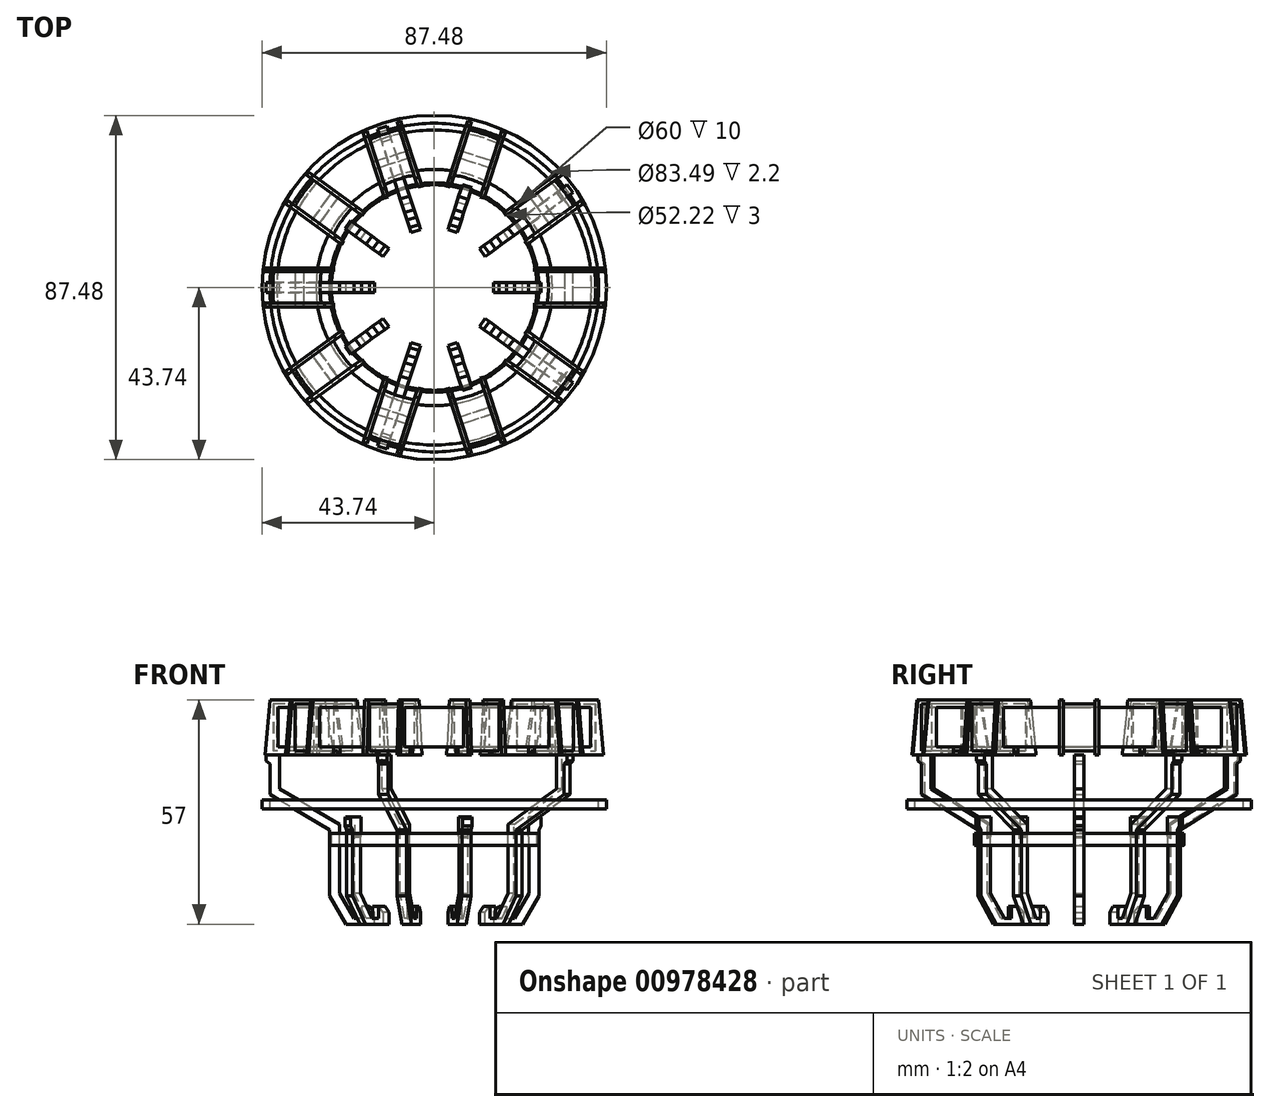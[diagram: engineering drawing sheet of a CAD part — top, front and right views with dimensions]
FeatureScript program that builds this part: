
annotation { "Feature Type Name" : "Feature", "Feature Type Description" : "" }
export const myFeature = defineFeature(function(context is Context, id is Id, definition is map)
    precondition{}
    {
        {
            var Q0;
            Q0=qCreatedBy(makeId("Top.planeOp"),FACE);
            var sketch = newSketch(context, id + "F0", { "sketchPlane" : qUnion([Q0])});
            skCircle(sketch, "E0", {"center": v(0, 0) * mm, "radius": 30 * mm});
            skCircle(sketch, "E1", {"center": v(0, 0) * mm, "radius": 40 * mm});
            skSolve(sketch);
        }
        {
            var Q0;
            Q0=makeQuery(id+"F0.imprint","IMPRINT",FACE,{"disambiguationData":[TD([[makeQuery(id+"F0.imprint","IMPRINT",EDGE,{"derivedFrom":sQuery(id+"F0.wireOp",EDGE,"E0")}),-1.0]])]});
            extrude(context, id + "F1", {"entities" : qUnion([Q0]), "depth" : 10 * mm, "offsetDistance" : 25 * mm});
        }
        {
            var Q0;
            Q0=qCreatedBy(makeId("Front.planeOp"),FACE);
            var sketch = newSketch(context, id + "F2", { "sketchPlane" : qUnion([Q0])});
            skLineSegment(sketch, "E2", {"start": v(-41.7, 12) * mm, "end": v(-27.87, 12) * mm});
            skLineSegment(sketch, "E3", {"start": v(-27.87, 12) * mm, "end": v(-25.51, -2) * mm});
            skLineSegment(sketch, "E4", {"start": v(-43.03, -2) * mm, "end": v(-41.7, 12) * mm});
            skLineSegment(sketch, "E5", {"start": v(-43.03, -2) * mm, "end": v(-35.17, -2) * mm});
            skLineSegment(sketch, "E6", {"start": v(-35.17, -2) * mm, "end": v(-35.17, 1.56) * mm});
            skLineSegment(sketch, "E7", {"start": v(-35.17, 1.56) * mm, "end": v(-33.24, 1.56) * mm});
            skLineSegment(sketch, "E8", {"start": v(-33.24, 1.56) * mm, "end": v(-33.24, -2) * mm});
            skLineSegment(sketch, "E9", {"start": v(-33.24, -2) * mm, "end": v(-25.51, -2) * mm});
            skSolve(sketch);
        }
        {
            var Q0;
            Q0 = qSketchRegion(id + "F2", true);
            extrude(context, id + "F3", {"entities" : qUnion([Q0]), "endBound" : BoundingType.SYMMETRIC, "depth" : 10 * mm, "offsetDistance" : 25 * mm});
        }
        {
            var Q0;
            Q0=makeQuery(id+"F1.opExtrude","SWEPT_BODY",BODY,{"disambiguationData":[OSD([sQuery(id+"F0.wireOp",EDGE,"E0"),sQuery(id+"F0.wireOp",EDGE,"E1")])]});
            var Q1;
            Q1=makeQuery(id+"F3.opExtrude","SWEPT_BODY",BODY,{"disambiguationData":[OSD([sQuery(id+"F2.wireOp",EDGE,"E2"),sQuery(id+"F2.wireOp",EDGE,"E3"),sQuery(id+"F2.wireOp",EDGE,"E4"),sQuery(id+"F2.wireOp",EDGE,"E5"),sQuery(id+"F2.wireOp",EDGE,"E6"),sQuery(id+"F2.wireOp",EDGE,"E7"),sQuery(id+"F2.wireOp",EDGE,"E8"),sQuery(id+"F2.wireOp",EDGE,"E9")])]});
            booleanBodies(context, id + "F4", {"operationType" : BooleanOperationType.SUBTRACTION, "tools" : qUnion([Q0]), "targets" : qUnion([Q1]), "keepTools" : true});
        }
        {
            var Q0;
            Q0=makeQuery(id+"F3.opExtrude","SWEPT_FACE",FACE,{"disambiguationData":[OSD([sQuery(id+"F2.wireOp",EDGE,"E2")])]});
            var Q1;
            Q1=makeQuery(id+"F3.opExtrude","SWEPT_FACE",FACE,{"disambiguationData":[OSD([sQuery(id+"F2.wireOp",EDGE,"E4")])]});
            var Q2;
            Q2=makeQuery(id+"F3.opExtrude","SWEPT_FACE",FACE,{"disambiguationData":[OSD([sQuery(id+"F2.wireOp",EDGE,"E5")])]});
            var Q3;
            Q3=makeQuery(id+"F3.opExtrude","SWEPT_FACE",FACE,{"disambiguationData":[OSD([sQuery(id+"F2.wireOp",EDGE,"E9")])]});
            var Q4;
            Q4=makeQuery(id+"F3.opExtrude","SWEPT_FACE",FACE,{"disambiguationData":[OSD([sQuery(id+"F2.wireOp",EDGE,"E3")])]});
            var Q5;
            Q5=makeQuery(id+"F3.opExtrude","SWEPT_FACE",FACE,{"disambiguationData":[OSD([sQuery(id+"F2.wireOp",EDGE,"E6")])]});
            var Q6;
            Q6=makeQuery(id+"F3.opExtrude","SWEPT_FACE",FACE,{"disambiguationData":[OSD([sQuery(id+"F2.wireOp",EDGE,"E8")])]});
            shell(context, id + "F5", {"entities" : qUnion([Q0, Q1, Q2, Q3, Q4, Q5, Q6]), "thickness" : 1 * mm});
        }
        {
            var Q0;
            Q0=makeQuery(id+"F3.opExtrude","SWEPT_BODY",BODY,{"disambiguationData":[OSD([sQuery(id+"F2.wireOp",EDGE,"E2"),sQuery(id+"F2.wireOp",EDGE,"E3"),sQuery(id+"F2.wireOp",EDGE,"E4"),sQuery(id+"F2.wireOp",EDGE,"E5"),sQuery(id+"F2.wireOp",EDGE,"E6"),sQuery(id+"F2.wireOp",EDGE,"E7"),sQuery(id+"F2.wireOp",EDGE,"E8"),sQuery(id+"F2.wireOp",EDGE,"E9")])]});
            var Q1;
            Q1=makeQuery(id+"F1.opExtrude","SWEPT_FACE",FACE,{"disambiguationData":[OSD([sQuery(id+"F0.wireOp",EDGE,"E0")])]});
            circularPattern(context, id + "F6", {"entities" : qUnion([Q0]), "axis" : qUnion([Q1]), "angle" : 360 * degree, "instanceCount" : 10, "equalSpace" : true});
        }
        {
            var Q0;
            Q0=qCreatedBy(makeId("Front.planeOp"),FACE);
            var sketch = newSketch(context, id + "F7", { "sketchPlane" : qUnion([Q0])});
            skLineSegment(sketch, "E10", {"start": v(15.1, -42) * mm, "end": v(15.1, -45) * mm});
            skLineSegment(sketch, "E11", {"start": v(15.1, -45) * mm, "end": v(22.45, -45) * mm});
            skLineSegment(sketch, "E12", {"start": v(22.45, -45) * mm, "end": v(26.6, -37.82) * mm});
            skLineSegment(sketch, "E13", {"start": v(26.6, -37.82) * mm, "end": v(26.6, -21.05) * mm});
            skLineSegment(sketch, "E14", {"start": v(26.6, -21.05) * mm, "end": v(27.15, -20.09) * mm});
            skLineSegment(sketch, "E15", {"start": v(27.15, -20.09) * mm, "end": v(27.15, -18.09) * mm});
            skLineSegment(sketch, "E16", {"start": v(26.96, -17.76) * mm, "end": v(27.15, -18.09) * mm});
            skLineSegment(sketch, "E17", {"start": v(26.96, -17.76) * mm, "end": v(23.96, -17.76) * mm});
            skLineSegment(sketch, "E18", {"start": v(15.1, -42) * mm, "end": v(16.42, -40.5) * mm});
            skLineSegment(sketch, "E19", {"start": v(16.42, -40.5) * mm, "end": v(18.42, -40.5) * mm});
            skLineSegment(sketch, "E20", {"start": v(18.42, -40.5) * mm, "end": v(18.42, -43.5) * mm});
            skLineSegment(sketch, "E21", {"start": v(24.1, -37.15) * mm, "end": v(24.1, -22.99) * mm});
            skLineSegment(sketch, "E22", {"start": v(24.1, -22.99) * mm, "end": v(23.96, -22.76) * mm});
            skLineSegment(sketch, "E23", {"start": v(23.96, -22.76) * mm, "end": v(23.96, -17.76) * mm});
            skLineSegment(sketch, "E24", {"start": v(18.42, -43.5) * mm, "end": v(20.42, -43.5) * mm});
            skLineSegment(sketch, "E25", {"start": v(20.42, -43.5) * mm, "end": v(24.1, -37.15) * mm});
            skLineSegment(sketch, "E26", {"start": v(-15.1, -45) * mm, "end": v(-15.1, -42) * mm});
            skLineSegment(sketch, "E27", {"start": v(-15.1, -42) * mm, "end": v(-16.42, -40.5) * mm});
            skLineSegment(sketch, "E28", {"start": v(-16.42, -40.5) * mm, "end": v(-18.42, -40.5) * mm});
            skLineSegment(sketch, "E29", {"start": v(-18.42, -40.5) * mm, "end": v(-18.42, -43.5) * mm});
            skLineSegment(sketch, "E30", {"start": v(-18.42, -43.5) * mm, "end": v(-20.42, -43.5) * mm});
            skLineSegment(sketch, "E31", {"start": v(-20.42, -43.5) * mm, "end": v(-24.1, -37.15) * mm});
            skLineSegment(sketch, "E32", {"start": v(-24.1, -37.15) * mm, "end": v(-24.1, -19.63) * mm});
            skLineSegment(sketch, "E33", {"start": v(-24.1, -19.63) * mm, "end": v(-39.24, -10.66) * mm});
            skLineSegment(sketch, "E34", {"start": v(-39.24, -10.66) * mm, "end": v(-39.24, -2) * mm});
            skLineSegment(sketch, "E35", {"start": v(-39.24, -2) * mm, "end": v(-42.68, -2) * mm});
            skLineSegment(sketch, "E36", {"start": v(-41.74, -4.3) * mm, "end": v(-41.74, -12.08) * mm});
            skLineSegment(sketch, "E37", {"start": v(-41.74, -12.08) * mm, "end": v(-26.6, -21.05) * mm});
            skLineSegment(sketch, "E38", {"start": v(-26.6, -21.05) * mm, "end": v(-26.6, -37.82) * mm});
            skLineSegment(sketch, "E39", {"start": v(-26.6, -37.82) * mm, "end": v(-22.45, -45) * mm});
            skLineSegment(sketch, "E40", {"start": v(-22.45, -45) * mm, "end": v(-15.1, -45) * mm});
            skLineSegment(sketch, "E41", {"start": v(-42.68, -2) * mm, "end": v(-42.68, -3.5) * mm});
            skLineSegment(sketch, "E42", {"start": v(-42.68, -3.5) * mm, "end": v(-41.74, -4.3) * mm});
            skSolve(sketch);
        }
        {
            var Q0;
            Q0=makeQuery(id+"F7.imprint","IMPRINT",FACE,{"disambiguationData":[TD([[makeQuery(id+"F7.imprint","IMPRINT",EDGE,{"derivedFrom":sQuery(id+"F7.wireOp",EDGE,"E10")}),1.0]])]});
            var Q1;
            Q1=makeQuery(id+"F7.imprint","IMPRINT",FACE,{"disambiguationData":[TD([[makeQuery(id+"F7.imprint","IMPRINT",EDGE,{"derivedFrom":sQuery(id+"F7.wireOp",EDGE,"E26")}),1.0]])]});
            extrude(context, id + "F8", {"entities" : qUnion([Q0, Q1]), "endBound" : BoundingType.SYMMETRIC, "depth" : 2.5 * mm, "offsetDistance" : 25 * mm});
        }
        {
            var Q0;
            Q0=makeQuery(id+"F8.opExtrude","SWEPT_BODY",BODY,{"disambiguationData":[OSD([sQuery(id+"F7.wireOp",EDGE,"E10"),sQuery(id+"F7.wireOp",EDGE,"E11"),sQuery(id+"F7.wireOp",EDGE,"E12"),sQuery(id+"F7.wireOp",EDGE,"E13"),sQuery(id+"F7.wireOp",EDGE,"E14"),sQuery(id+"F7.wireOp",EDGE,"E15"),sQuery(id+"F7.wireOp",EDGE,"E16"),sQuery(id+"F7.wireOp",EDGE,"E17"),sQuery(id+"F7.wireOp",EDGE,"E18"),sQuery(id+"F7.wireOp",EDGE,"E19"),sQuery(id+"F7.wireOp",EDGE,"E20"),sQuery(id+"F7.wireOp",EDGE,"E21"),sQuery(id+"F7.wireOp",EDGE,"E22"),sQuery(id+"F7.wireOp",EDGE,"E23"),sQuery(id+"F7.wireOp",EDGE,"E24"),sQuery(id+"F7.wireOp",EDGE,"E25")])]});
            var Q1;
            Q1=makeQuery(id+"F8.opExtrude","SWEPT_BODY",BODY,{"disambiguationData":[OSD([sQuery(id+"F7.wireOp",EDGE,"E26"),sQuery(id+"F7.wireOp",EDGE,"E27"),sQuery(id+"F7.wireOp",EDGE,"E28"),sQuery(id+"F7.wireOp",EDGE,"E29"),sQuery(id+"F7.wireOp",EDGE,"E30"),sQuery(id+"F7.wireOp",EDGE,"E31"),sQuery(id+"F7.wireOp",EDGE,"E32"),sQuery(id+"F7.wireOp",EDGE,"E33"),sQuery(id+"F7.wireOp",EDGE,"E34"),sQuery(id+"F7.wireOp",EDGE,"E35"),sQuery(id+"F7.wireOp",EDGE,"ou7bWfvp-Nuvi-0B3R-6LIp-XRIRuBnvQizE"),sQuery(id+"F7.wireOp",EDGE,"mc10MxTr-XRXP-W1Zo-hVJU-oox8hIU6NUmr"),sQuery(id+"F7.wireOp",EDGE,"E36"),sQuery(id+"F7.wireOp",EDGE,"E37"),sQuery(id+"F7.wireOp",EDGE,"E38"),sQuery(id+"F7.wireOp",EDGE,"E39"),sQuery(id+"F7.wireOp",EDGE,"E40")])]});
            var Q2;
            Q2=makeQuery(id+"F1.opExtrude","CAP_EDGE",EDGE,{"disambiguationData":[OSD([sQuery(id+"F0.wireOp",EDGE,"E0")])],"isStart":true});
            circularPattern(context, id + "F9", {"entities" : qUnion([Q0, Q1]), "axis" : qUnion([Q2]), "angle" : 360 * degree, "instanceCount" : 5, "equalSpace" : true});
        }
        {
            var Q0;
            Q0=qCreatedBy(makeId("Top.planeOp"),FACE);
            var sketch = newSketch(context, id + "F10", { "sketchPlane" : qUnion([Q0])});
            skCircle(sketch, "E43", {"center": v(0, 0) * mm, "radius": 26.6 * mm});
            skCircle(sketch, "E44", {"center": v(0, 0) * mm, "radius": 26.1 * mm});
            skSolve(sketch);
        }
        {
            var Q0;
            Q0 = qSketchRegion(id + "F10", true);
            extrude(context, id + "F11", {"entities" : qUnion([Q0]), "oppositeDirection" : true, "depth" : 25 * mm, "offsetDistance" : 25 * mm, "hasSecondDirection" : true, "secondDirectionOppositeDirection" : true, "secondDirectionDepth" : 22 * mm});
        }
        {
            var Q0;
            Q0=qCreatedBy(makeId("Top.planeOp"),FACE);
            var sketch = newSketch(context, id + "F12", { "sketchPlane" : qUnion([Q0])});
            skCircle(sketch, "E45", {"center": v(0, 0) * mm, "radius": 41.74 * mm});
            skCircle(sketch, "E46", {"center": v(0, 0) * mm, "radius": 43.74 * mm});
            skSolve(sketch);
        }
        {
            var Q0;
            Q0 = qSketchRegion(id + "F12", true);
            extrude(context, id + "F13", {"entities" : qUnion([Q0]), "oppositeDirection" : true, "depth" : 15.7 * mm, "offsetDistance" : 25 * mm, "hasSecondDirection" : true, "secondDirectionOppositeDirection" : true, "secondDirectionDepth" : 13.5 * mm});
        }
    });
